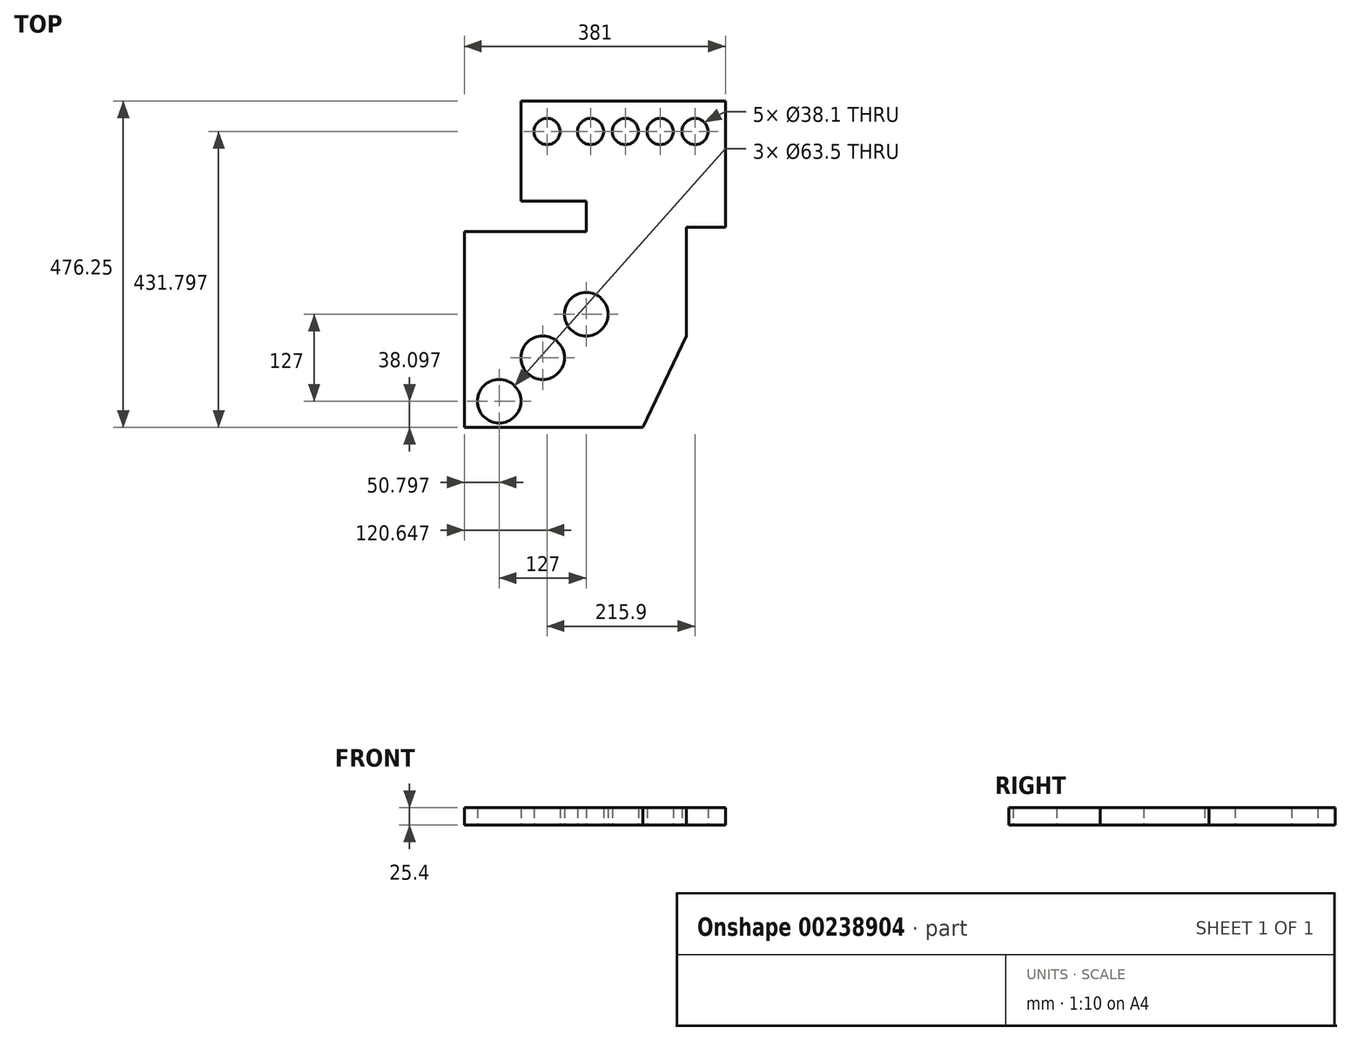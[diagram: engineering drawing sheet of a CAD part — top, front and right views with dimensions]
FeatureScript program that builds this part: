
annotation { "Feature Type Name" : "Feature", "Feature Type Description" : "" }
export const myFeature = defineFeature(function(context is Context, id is Id, definition is map)
    precondition{}
    {
        {
            var Q0;
            Q0=qCreatedBy(makeId("Top.planeOp"),FACE);
            var sketch = newSketch(context, id + "F0", { "sketchPlane" : qUnion([Q0])});
            skLineSegment(sketch, "E0", {"start": v(-159.1, -99.1) * mm, "end": v(-159.1, 186.66) * mm});
            skLineSegment(sketch, "E1", {"start": v(-159.1, 186.66) * mm, "end": v(18.7, 186.66) * mm});
            skLineSegment(sketch, "E2", {"start": v(18.7, 186.66) * mm, "end": v(18.7, 231.1) * mm});
            skLineSegment(sketch, "E3", {"start": v(18.7, 231.1) * mm, "end": v(-76.54, 231.1) * mm});
            skLineSegment(sketch, "E4", {"start": v(-76.54, 231.1) * mm, "end": v(-76.54, 377.16) * mm});
            skLineSegment(sketch, "E5", {"start": v(-76.54, 377.16) * mm, "end": v(221.9, 377.16) * mm});
            skLineSegment(sketch, "E6", {"start": v(221.9, 377.16) * mm, "end": v(221.9, 193) * mm});
            skLineSegment(sketch, "E7", {"start": v(221.9, 193) * mm, "end": v(164.76, 193) * mm});
            skLineSegment(sketch, "E8", {"start": v(164.76, 193) * mm, "end": v(164.76, 34.26) * mm});
            skLineSegment(sketch, "E9", {"start": v(164.76, 34.26) * mm, "end": v(101.26, -99.1) * mm});
            skLineSegment(sketch, "E10", {"start": v(221.9, 377.16) * mm, "end": v(177.46, 377.16) * mm});
            skCircle(sketch, "E11", {"center": v(177.46, 332.7) * mm, "radius": 19.05 * mm});
            skCircle(sketch, "E12", {"center": v(126.66, 332.7) * mm, "radius": 19.05 * mm});
            skCircle(sketch, "E13", {"center": v(75.86, 332.7) * mm, "radius": 19.05 * mm});
            skCircle(sketch, "E14", {"center": v(25.06, 332.7) * mm, "radius": 19.05 * mm});
            skCircle(sketch, "E15", {"center": v(-38.44, 332.7) * mm, "radius": 19.05 * mm});
            skCircle(sketch, "E16", {"center": v(-108.3, -61) * mm, "radius": 31.75 * mm});
            skPoint(sketch, "E17.start.orphan", {"position": v(-28.92, -99.1) * mm});
            skCircle(sketch, "E18", {"center": v(-44.8, 2.5) * mm, "radius": 31.75 * mm});
            skCircle(sketch, "E19", {"center": v(18.7, 66) * mm, "radius": 31.75 * mm});
            skLineSegment(sketch, "E20", {"start": v(-159.1, -99.1) * mm, "end": v(101.26, -99.1) * mm});
            skSolve(sketch);
        }
        {
            var Q0;
            Q0 = qSketchRegion(id + "F0", true);
            extrude(context, id + "F1", {"entities" : qUnion([Q0]), "depth" : 25.4 * mm});
        }
    });
